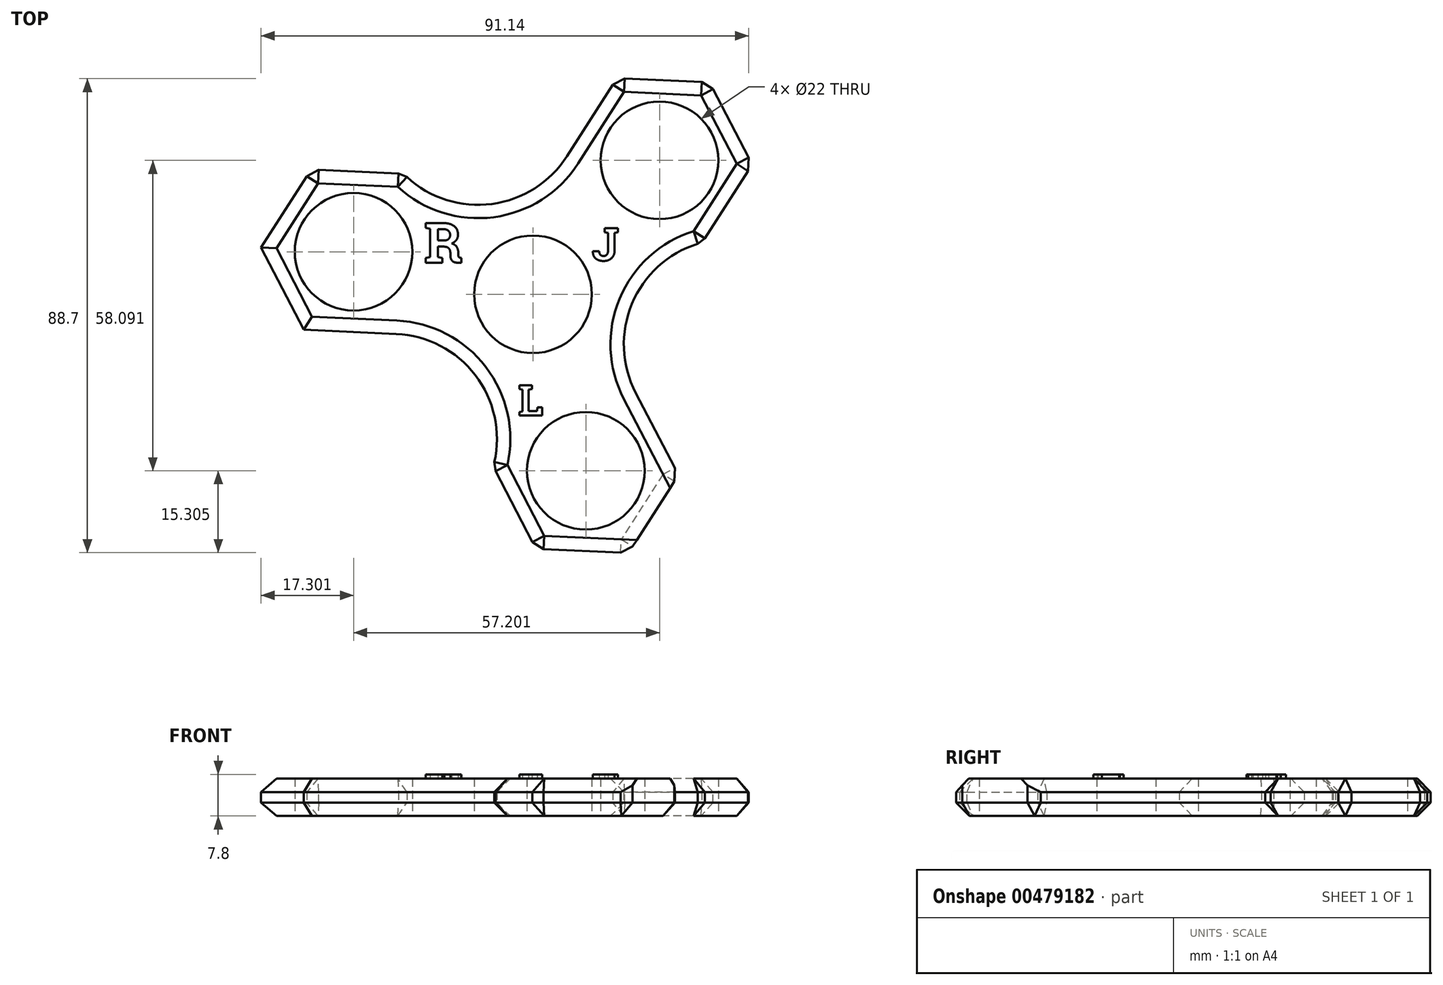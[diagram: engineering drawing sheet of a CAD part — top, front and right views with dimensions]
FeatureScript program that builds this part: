
annotation { "Feature Type Name" : "Feature", "Feature Type Description" : "" }
export const myFeature = defineFeature(function(context is Context, id is Id, definition is map)
    precondition{}
    {
        {
            var Q0;
            Q0=qCreatedBy(makeId("Top.planeOp"),FACE);
            var sketch = newSketch(context, id + "F0", { "sketchPlane" : qUnion([Q0])});
            skCircle(sketch, "E0", {"center": v(0, 0) * mm, "radius": 11 * mm});
            skCircle(sketch, "E1", {"center": v(0, 0) * mm, "radius": 15 * mm});
            skCircle(sketch, "E2", {"center": v(23.66, 25.07) * mm, "radius": 11 * mm});
            skCircle(sketch, "E3.1.0", {"center": v(-33.54, 7.96) * mm, "radius": 11 * mm});
            skCircle(sketch, "E3.2.0", {"center": v(9.88, -33.02) * mm, "radius": 11 * mm});
            skCircle(sketch, "E4.cCircle", {"center": v(-33.54, 7.96) * mm, "radius": 15 * mm, "construction": true});
            skLineSegment(sketch, "E4.0", {"start": v(-24.21, 22.56) * mm, "end": v(-16.24, 7.18) * mm});
            skLineSegment(sketch, "E4.1", {"start": v(-16.24, 7.18) * mm, "end": v(-25.56, -7.41) * mm});
            skLineSegment(sketch, "E4.2", {"start": v(-25.56, -7.41) * mm, "end": v(-42.86, -6.64) * mm});
            skLineSegment(sketch, "E4.3", {"start": v(-42.86, -6.64) * mm, "end": v(-50.84, 8.74) * mm});
            skLineSegment(sketch, "E4.4", {"start": v(-50.84, 8.74) * mm, "end": v(-41.52, 23.33) * mm});
            skLineSegment(sketch, "E4.5", {"start": v(-41.52, 23.33) * mm, "end": v(-24.21, 22.56) * mm});
            skPoint(sketch, "E4.0.midPoint", {"position": v(-20.22, 14.87) * mm});
            skLineSegment(sketch, "E5.1.0", {"start": v(0.55, -47.62) * mm, "end": v(-7.43, -32.25) * mm});
            skLineSegment(sketch, "E5.1.1", {"start": v(-7.43, -32.25) * mm, "end": v(1.9, -17.65) * mm});
            skLineSegment(sketch, "E5.1.2", {"start": v(1.9, -17.65) * mm, "end": v(19.2, -18.43) * mm});
            skCircle(sketch, "E5.1.3", {"center": v(9.88, -33.02) * mm, "radius": 15 * mm, "construction": true});
            skLineSegment(sketch, "E5.1.4", {"start": v(19.2, -18.43) * mm, "end": v(27.18, -33.8) * mm});
            skLineSegment(sketch, "E5.1.5", {"start": v(27.18, -33.8) * mm, "end": v(17.86, -48.4) * mm});
            skLineSegment(sketch, "E5.1.6", {"start": v(17.86, -48.4) * mm, "end": v(0.55, -47.62) * mm});
            skLineSegment(sketch, "E5.2.0", {"start": v(40.97, 24.29) * mm, "end": v(31.64, 9.7) * mm});
            skLineSegment(sketch, "E5.2.1", {"start": v(31.64, 9.7) * mm, "end": v(14.34, 10.47) * mm});
            skLineSegment(sketch, "E5.2.2", {"start": v(14.34, 10.47) * mm, "end": v(6.36, 25.84) * mm});
            skCircle(sketch, "E5.2.3", {"center": v(23.66, 25.07) * mm, "radius": 15 * mm, "construction": true});
            skLineSegment(sketch, "E5.2.4", {"start": v(6.36, 25.84) * mm, "end": v(15.68, 40.44) * mm});
            skLineSegment(sketch, "E5.2.5", {"start": v(15.68, 40.44) * mm, "end": v(32.99, 39.66) * mm});
            skLineSegment(sketch, "E5.2.6", {"start": v(32.99, 39.66) * mm, "end": v(40.97, 24.29) * mm});
            skArc(sketch, "E6", {"start": v(-24.21, 22.56) * mm, "mid": v(-8.14, 16.86) * mm, "end": v(6.36, 25.84) * mm});
            skArc(sketch, "E7.1.0", {"start": v(-7.43, -32.25) * mm, "mid": v(-10.53, -15.48) * mm, "end": v(-25.56, -7.41) * mm});
            skArc(sketch, "E7.2.0", {"start": v(31.64, 9.7) * mm, "mid": v(18.67, -1.38) * mm, "end": v(19.2, -18.43) * mm});
            skSolve(sketch);
        }
        {
            var Q0;
            Q0=makeQuery(id+"F0.imprint","IMPRINT",FACE,{"disambiguationData":[TD([[makeQuery(id+"F0.imprint","IMPRINT",EDGE,{"derivedFrom":sQuery(id+"F0.wireOp",EDGE,"E3.1.0")}),-1.0]])]});
            var Q1;
            Q1=makeQuery(id+"F0.imprint","IMPRINT",FACE,{"disambiguationData":[TD([[makeQuery(id+"F0.imprint","IMPRINT",EDGE,{"derivedFrom":sQuery(id+"F0.wireOp",EDGE,"E0")}),-1.0]])]});
            var Q2;
            Q2=makeQuery(id+"F0.imprint","IMPRINT",FACE,{"disambiguationData":[TD([[makeQuery(id+"F0.imprint","IMPRINT",EDGE,{"derivedFrom":sQuery(id+"F0.wireOp",EDGE,"E1")}),-1.0]])]});
            var Q3;
            Q3=makeQuery(id+"F0.imprint","IMPRINT",FACE,{"disambiguationData":[TD([[makeQuery(id+"F0.imprint","IMPRINT",EDGE,{"derivedFrom":sQuery(id+"F0.wireOp",EDGE,"E2")}),-1.0]])]});
            var Q4;
            Q4=makeQuery(id+"F0.imprint","IMPRINT",FACE,{"disambiguationData":[TD([[makeQuery(id+"F0.imprint","IMPRINT",EDGE,{"derivedFrom":sQuery(id+"F0.wireOp",EDGE,"E3.2.0")}),-1.0]])]});
            extrude(context, id + "F1", {"entities" : qUnion([Q0, Q1, Q2, Q3, Q4]), "depth" : 7 * mm});
        }
        {
            var Q0;
            Q0=makeQuery(id+"F1.opExtrude","CAP_EDGE",EDGE,{"disambiguationData":[OSD([sQuery(id+"F0.wireOp",EDGE,"E4.4")])],"isStart":false});
            var Q1;
            Q1=makeQuery(id+"F1.opExtrude","CAP_EDGE",EDGE,{"disambiguationData":[OSD([sQuery(id+"F0.wireOp",EDGE,"E4.3")])],"isStart":false});
            var Q2;
            Q2=makeQuery(id+"F1.opExtrude","CAP_EDGE",EDGE,{"disambiguationData":[OSD([sQuery(id+"F0.wireOp",EDGE,"E4.3")])],"isStart":true});
            var Q3;
            Q3=makeQuery(id+"F1.opExtrude","CAP_EDGE",EDGE,{"disambiguationData":[OSD([sQuery(id+"F0.wireOp",EDGE,"E4.4")])],"isStart":true});
            var Q4;
            Q4=makeQuery(id+"F1.opExtrude","CAP_EDGE",EDGE,{"disambiguationData":[OSD([sQuery(id+"F0.wireOp",EDGE,"E4.2")])],"isStart":true});
            var Q5;
            Q5=makeQuery(id+"F1.opExtrude","CAP_EDGE",EDGE,{"disambiguationData":[OSD([sQuery(id+"F0.wireOp",EDGE,"E4.2")])],"isStart":false});
            var Q6;
            Q6=makeQuery(id+"F1.opExtrude","SWEPT_FACE",FACE,{"disambiguationData":[OSD([sQuery(id+"F0.wireOp",EDGE,"E4.5")])]});
            var Q7;
            Q7=makeQuery(id+"F1.opExtrude","CAP_EDGE",EDGE,{"disambiguationData":[OSD([sQuery(id+"F0.wireOp",EDGE,"E6")])],"isStart":true});
            var Q8;
            Q8=makeQuery(id+"F1.opExtrude","SWEPT_FACE",FACE,{"disambiguationData":[OSD([sQuery(id+"F0.wireOp",EDGE,"E6")])]});
            var Q9;
            Q9=makeQuery(id+"F1.opExtrude","SWEPT_FACE",FACE,{"disambiguationData":[OSD([sQuery(id+"F0.wireOp",EDGE,"E5.2.5")])]});
            var Q10;
            Q10=makeQuery(id+"F1.opExtrude","SWEPT_FACE",FACE,{"disambiguationData":[OSD([sQuery(id+"F0.wireOp",EDGE,"E5.2.0")])]});
            var Q11;
            Q11=makeQuery(id+"F1.opExtrude","SWEPT_FACE",FACE,{"disambiguationData":[OSD([sQuery(id+"F0.wireOp",EDGE,"E5.2.6")])]});
            var Q12;
            Q12=makeQuery(id+"F1.opExtrude","SWEPT_FACE",FACE,{"disambiguationData":[OSD([sQuery(id+"F0.wireOp",EDGE,"E7.2.0")])]});
            var Q13;
            Q13=makeQuery(id+"F1.opExtrude","SWEPT_FACE",FACE,{"disambiguationData":[OSD([sQuery(id+"F0.wireOp",EDGE,"E5.1.4")])]});
            var Q14;
            Q14=makeQuery(id+"F1.opExtrude","CAP_EDGE",EDGE,{"disambiguationData":[OSD([sQuery(id+"F0.wireOp",EDGE,"E5.1.5")])],"isStart":true});
            var Q15;
            Q15=makeQuery(id+"F1.opExtrude","SWEPT_FACE",FACE,{"disambiguationData":[OSD([sQuery(id+"F0.wireOp",EDGE,"E5.1.6")])]});
            var Q16;
            Q16=makeQuery(id+"F1.opExtrude","SWEPT_FACE",FACE,{"disambiguationData":[OSD([sQuery(id+"F0.wireOp",EDGE,"E5.1.0")])]});
            chamfer(context, id + "F2", {"entities" : qUnion([Q0, Q1, Q2, Q3, Q4, Q5, Q6, Q7, Q8, Q9, Q10, Q11, Q12, Q13, Q14, Q15, Q16]), "width" : 2.5 * mm, "tangentPropagation" : true});
        }
        {
            var Q0;
            Q0=makeQuery(id+"F1.opExtrude","CAP_FACE",FACE,{"disambiguationData":[OSD([sQuery(id+"F0.wireOp",EDGE,"E0"),sQuery(id+"F0.wireOp",EDGE,"E2"),sQuery(id+"F0.wireOp",EDGE,"E3.1.0"),sQuery(id+"F0.wireOp",EDGE,"E3.2.0"),sQuery(id+"F0.wireOp",EDGE,"E4.2"),sQuery(id+"F0.wireOp",EDGE,"E4.3"),sQuery(id+"F0.wireOp",EDGE,"E4.4"),sQuery(id+"F0.wireOp",EDGE,"E4.5"),sQuery(id+"F0.wireOp",EDGE,"E5.1.0"),sQuery(id+"F0.wireOp",EDGE,"E5.1.4"),sQuery(id+"F0.wireOp",EDGE,"E5.1.5"),sQuery(id+"F0.wireOp",EDGE,"E5.1.6"),sQuery(id+"F0.wireOp",EDGE,"E5.2.0"),sQuery(id+"F0.wireOp",EDGE,"E5.2.4"),sQuery(id+"F0.wireOp",EDGE,"E5.2.5"),sQuery(id+"F0.wireOp",EDGE,"E5.2.6"),sQuery(id+"F0.wireOp",EDGE,"E6"),sQuery(id+"F0.wireOp",EDGE,"E7.1.0"),sQuery(id+"F0.wireOp",EDGE,"E7.2.0")])],"isStart":false});
            var sketch = newSketch(context, id + "F3", { "sketchPlane" : qUnion([Q0])});
            skText(sketch, "E8", { "text": "J", "fontName": "RobotoSlab-Bold.ttf"});
            skText(sketch, "E9", { "text": "L", "fontName": "RobotoSlab-Bold.ttf"});
            skText(sketch, "E10", { "text": "R", "fontName": "RobotoSlab-Bold.ttf"});
            const initialGuessF3  = {"E8": [0.01105, 0.00632, 1, 0, 0.00612], "E9": [-0.00276, -0.0227, 1, 0, 0.00572], "E10": [-0.02033, 0.00592, 1, 0, 0.0075]};
            skSetInitialGuess(sketch, initialGuessF3);
            skSolve(sketch);
        }
        {
            var Q0;
            Q0=makeQuery(id+"F3.imprint","IMPRINT",FACE,{"disambiguationData":[TD([[makeQuery(id+"F3.imprint","IMPRINT",EDGE,{"derivedFrom":sQuery(id+"F3.wireOp",EDGE,"E10.sketch_text.stroke-0")}),-1.0]])]});
            var Q1;
            Q1=makeQuery(id+"F3.imprint","IMPRINT",FACE,{"disambiguationData":[TD([[makeQuery(id+"F3.imprint","IMPRINT",EDGE,{"derivedFrom":sQuery(id+"F3.wireOp",EDGE,"E9.sketch_text.stroke-0")}),-1.0]])]});
            var Q2;
            Q2=makeQuery(id+"F3.imprint","IMPRINT",FACE,{"disambiguationData":[TD([[makeQuery(id+"F3.imprint","IMPRINT",EDGE,{"derivedFrom":sQuery(id+"F3.wireOp",EDGE,"E8.sketch_text.stroke-0")}),-1.0]])]});
            extrude(context, id + "F4", {"entities" : qUnion([Q0, Q1, Q2]), "operationType" : NewBodyOperationType.ADD, "depth" : 0.8 * mm});
        }
    });
